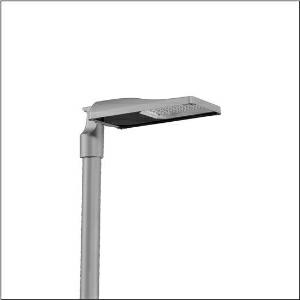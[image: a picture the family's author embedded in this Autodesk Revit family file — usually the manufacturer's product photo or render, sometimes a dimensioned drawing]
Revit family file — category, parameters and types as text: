
# Revit family: streetlight_sl_31_mini___st1_0a_5xh2d71b08ja_2c97
name_source: partatom
category: Lighting Fixtures
units: mm (PartAtom-declared; Revit-internal decimal feet)

## family parameters
Cut with Voids When Loaded = No
Host = Face
Light Source = No
Part Type = Normal
Room Calculation Point = No
Round Connector Dimension = Use Diameter
Shared = No

## types (1)
- --- (1 x LED, 9800 lm, 81.1 W, 2200K)
    Apparent Load = 81 VA
    CIE Flux Codes = 40 73 97 100 100
    Color Rendering = 70
    Color Temperature = 2200K
    Default Elevation = 1800 mm
    Description = Streetlight SL 31 mini Easy, LST, Desk-Remote mast luminaire for post-top, side-entry; light control with lens of PMMA; light distribution: ST1.0a, direct asymmetric distribution, for standard-compliant lighting for roads and squares; LED: luminous flux: 9.800lm, light colour: 722, colour temperature: 2200K; luminous efficacy: 120,8lm/W; control: pre-setting: linear dimming characteristic, flexible luminous flux parameterisation, time-dependent luminous flux control, constant luminous flux control, power reduction, intelligent temperature release in ECG and LED module, overheat protection; luminaire housing, of diecast aluminium, SITECO metallic grey (DB 702S), corrosivity category C5 high according to DIN EN ISO 12944; cover of toughened safety glass, transparent, mast flange of diecast aluminium, SITECO metallic grey (DB 702S), spigot size: 76/60mm, mast flange included unmounted; cable length: 10,5m, connection cable pre-assembled; mains connection: 220..240V, AC, 50/60Hz; power consumption (at start of service life): 81,1W / (at end of service life): 88,3W / (with reduced operation 50%): 36,1W; protection rating (complete): IP66; insulation class (complete): insulation class II (safety insulation); impact resistance: IK10; certification: CE, ENEC, ENEC+, VDE, UKCA; permissible operating ambient temperature for outdoor applications: -40..+50°C; packaging unit: 1 piece

Light Distribution: ST1.0a
    Height = 76 mm
    Lamp = 1 x LED
    Lamp Light Flux = 9800 lm
    Lamp Power = 81.1 W
    Lamp count = 1
    Length = 547 mm
    Luminous efficacy = 121 lm/W
    Manufacturer = Siteco
    ModVariant = No
    Model = 5XH2D71B08JA
    Number of Poles = 1
    OnlyDefault = Yes
    Power Factor = 1
    Product Name = Streetlight SL 31 mini | ST1.0a
    Product group = mast luminaire | pylon top
    ProductGroupID = 6100
    Protection Class = Protection class II
    Protection Degree = IP 66
    RLX_Detail_Level = 1
    RLX_Emergency_Light_Flux = 0 lm
    RLX_Emergency_Type = 0
    RLX_Emergency_Type_DB = No
    RlxData = <blob elided: 39605 chars, md5=e9e7a118>
    Socket = socket
    Standby Power = 0 W
    System Light Flux = 9800 lm
    System Power = 81 W
    Type Comments = factory setting: luminous flux: 100 % | dim-lin: 254 | 860 mA
    Type Image = l_1300326.jpg
    URL = http://relux.com
    VarID = @adj_009243
    Voltage = 0 V
    Weight = 0.00 kg
    Width = 265 mm

## geometry (parser evidence)
native form markers: Blend x4, Sweep x9
no freeform markers — native parametric forms only
